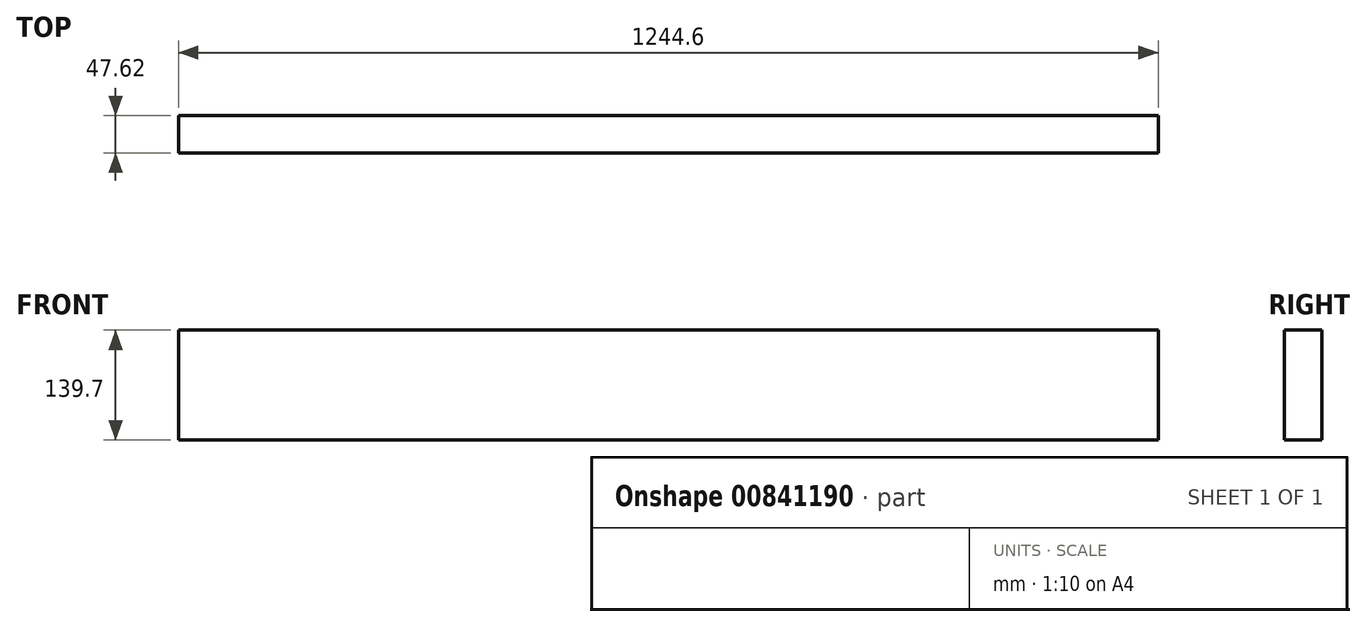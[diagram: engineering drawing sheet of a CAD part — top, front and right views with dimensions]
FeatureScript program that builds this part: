
annotation { "Feature Type Name" : "Feature", "Feature Type Description" : "" }
export const myFeature = defineFeature(function(context is Context, id is Id, definition is map)
    precondition{}
    {
        {
            var Q0;
            Q0=qCreatedBy(makeId("Right.planeOp"),FACE);
            var sketch = newSketch(context, id + "F0", { "sketchPlane" : qUnion([Q0])});
            skLineSegment(sketch, "E0.bottom", {"start": v(0, 0) * mm, "end": v(47.62, 0) * mm});
            skLineSegment(sketch, "E0.top", {"start": v(0, -139.7) * mm, "end": v(47.63, -139.7) * mm});
            skLineSegment(sketch, "E0.left", {"start": v(0, 0) * mm, "end": v(0, -139.7) * mm});
            skLineSegment(sketch, "E0.right", {"start": v(47.62, 0) * mm, "end": v(47.63, -139.7) * mm});
            skSolve(sketch);
        }
        {
            var Q0;
            Q0=qSketchRegion(id+"F0",true);
            extrude(context, id + "F1", {"entities" : qUnion([Q0]), "depth" : 1244.6 * mm, "offsetDistance" : 25.4 * mm});
        }
    });
